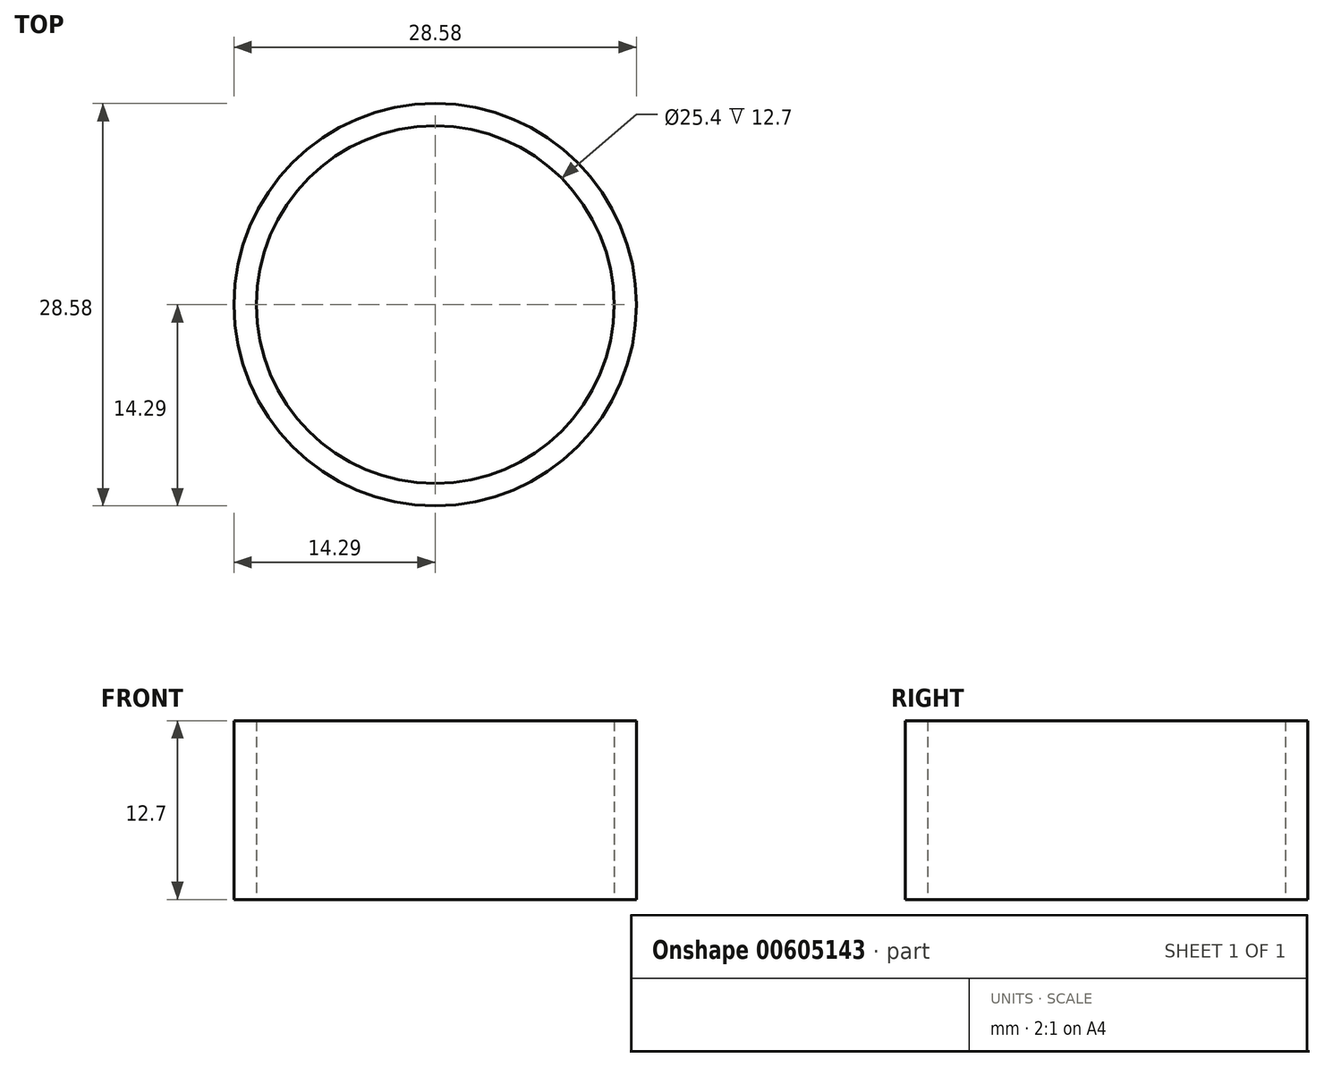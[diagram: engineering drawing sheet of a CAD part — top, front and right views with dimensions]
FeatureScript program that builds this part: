
annotation { "Feature Type Name" : "Feature", "Feature Type Description" : "" }
export const myFeature = defineFeature(function(context is Context, id is Id, definition is map)
    precondition{}
    {
        {
            var Q0;
            Q0=qCreatedBy(makeId("Top.planeOp"),FACE);
            var sketch = newSketch(context, id + "F0", { "sketchPlane" : qUnion([Q0])});
            skLineSegment(sketch, "E0", {"start": v(0, 0) * mm, "end": v(12.7, 0) * mm});
            skCircle(sketch, "E1", {"center": v(0, 0) * mm, "radius": 12.7 * mm});
            skCircle(sketch, "E2.0", {"center": v(0, 0) * mm, "radius": 14.29 * mm});
            skSolve(sketch);
        }
        {
            var Q0;
            Q0=qCreatedBy(makeId("Top.planeOp"),FACE);
            var sketch = newSketch(context, id + "F1", { "sketchPlane" : qUnion([Q0])});
            skSolve(sketch);
        }
        {
            var Q0;
            Q0=qSketchRegion(id+"F1",true);
            var Q1;
            Q1=makeQuery(id+"F0.imprint","IMPRINT",FACE,{"disambiguationData":[TD([[makeQuery(id+"F0.imprint","IMPRINT",EDGE,{"derivedFrom":sQuery(id+"F0.wireOp",EDGE,"E1")}),-1.0]])]});
            extrude(context, id + "F2", {"entities" : qUnion([Q0, Q1]), "depth" : 12.7 * mm, "offsetDistance" : 25.4 * mm});
        }
    });
